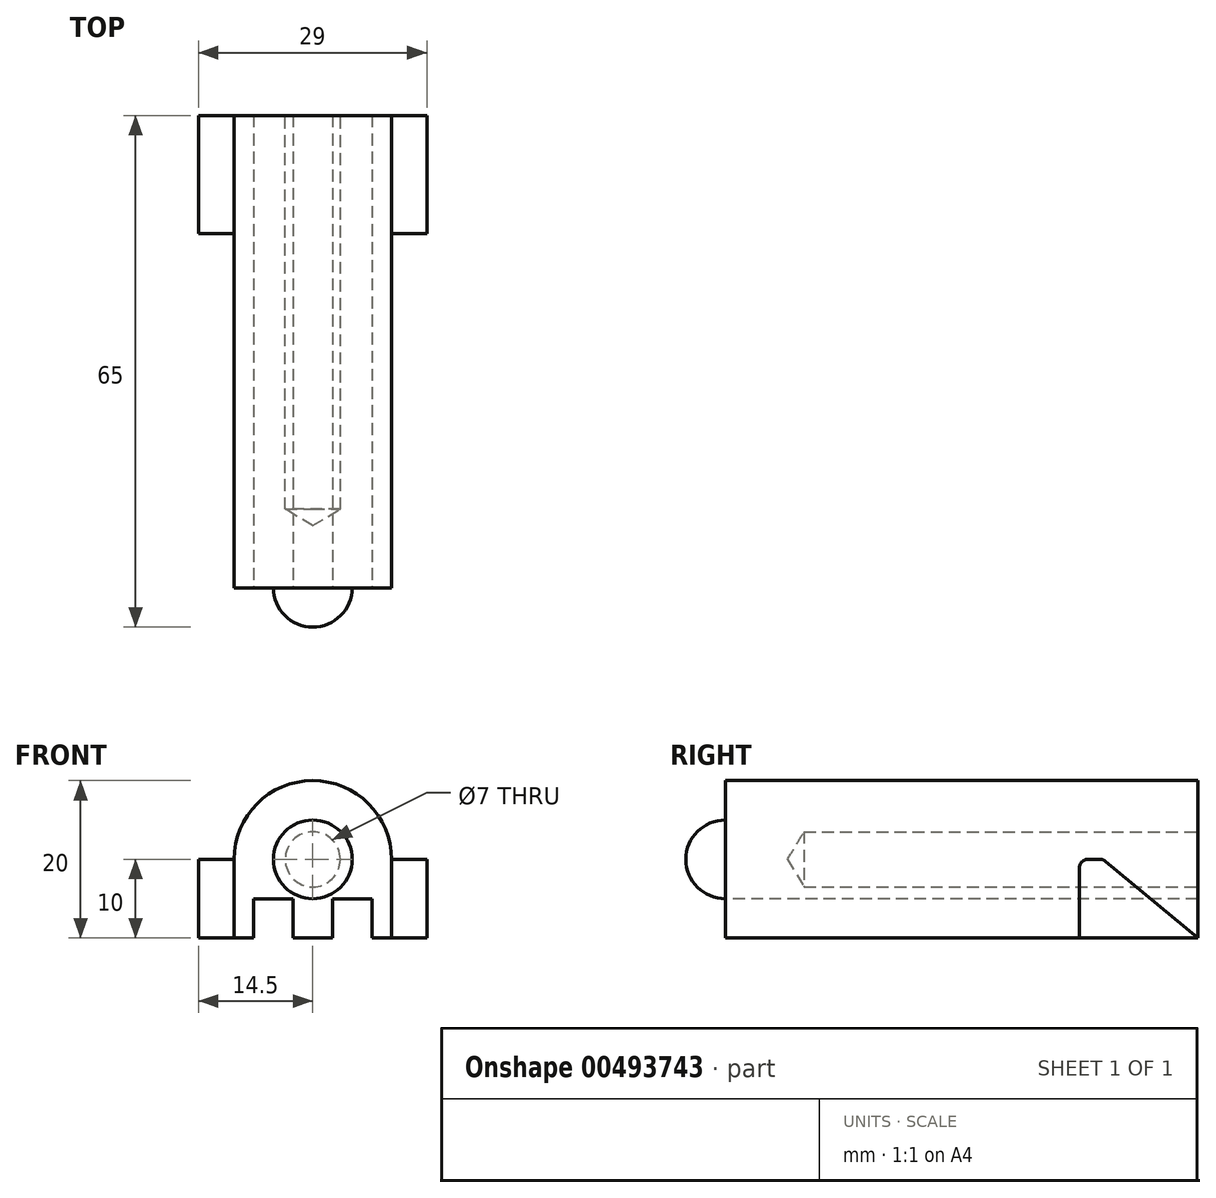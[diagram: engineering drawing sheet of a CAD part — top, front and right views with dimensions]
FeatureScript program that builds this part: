
annotation { "Feature Type Name" : "Feature", "Feature Type Description" : "" }
export const myFeature = defineFeature(function(context is Context, id is Id, definition is map)
    precondition{}
    {
        {
            var Q0;
            Q0=qCreatedBy(makeId("Front.planeOp"),FACE);
            var sketch = newSketch(context, id + "F0", { "sketchPlane" : qUnion([Q0])});
            skLineSegment(sketch, "E0.bottom", {"start": v(-10, 0) * mm, "end": v(-7.5, 0) * mm});
            skLineSegment(sketch, "E0.left", {"start": v(-10, 0) * mm, "end": v(-10, 10) * mm});
            skLineSegment(sketch, "E0.right", {"start": v(10, 0) * mm, "end": v(10, 10) * mm});
            skArc(sketch, "E1", {"start": v(10, 10) * mm, "mid": v(0, 20) * mm, "end": v(-10, 10) * mm});
            skLineSegment(sketch, "E2.top", {"start": v(-2.5, 5) * mm, "end": v(-7.5, 5) * mm});
            skLineSegment(sketch, "E2.left", {"start": v(-2.5, 0) * mm, "end": v(-2.5, 5) * mm});
            skLineSegment(sketch, "E2.right", {"start": v(-7.5, 0) * mm, "end": v(-7.5, 5) * mm});
            skLineSegment(sketch, "E3.bottom", {"start": v(2.5, 5) * mm, "end": v(7.5, 5) * mm});
            skLineSegment(sketch, "E3.left", {"start": v(2.5, 5) * mm, "end": v(2.5, 0) * mm});
            skLineSegment(sketch, "E3.right", {"start": v(7.5, 5) * mm, "end": v(7.5, 0) * mm});
            skLineSegment(sketch, "E4.trimOffspring", {"start": v(7.5, 0) * mm, "end": v(10, 0) * mm});
            skLineSegment(sketch, "E5.trimOffspring", {"start": v(-2.5, 0) * mm, "end": v(2.5, 0) * mm});
            skSolve(sketch);
        }
        {
            var Q0;
            Q0 = qSketchRegion(id + "F0", true);
            extrude(context, id + "F1", {"entities" : qUnion([Q0]), "oppositeDirection" : true, "depth" : 60 * mm});
        }
        {
            var Q0;
            Q0=qCreatedBy(makeId("Right.planeOp"),FACE);
            var sketch = newSketch(context, id + "F2", { "sketchPlane" : qUnion([Q0])});
            skArc(sketch, "E6", {"start": v(0, 15) * mm, "mid": v(-5, 10) * mm, "end": v(0, 5) * mm});
            skLineSegment(sketch, "E7", {"start": v(0, 15) * mm, "end": v(0, 5) * mm});
            skSolve(sketch);
        }
        {
            var Q0;
            Q0=makeQuery(id+"F2.imprint","IMPRINT",FACE,{"disambiguationData":[TD([[makeQuery(id+"F2.imprint","IMPRINT",EDGE,{"derivedFrom":sQuery(id+"F2.wireOp",EDGE,"E6")}),1.0]])]});
            var Q1;
            Q1=sQuery(id+"F2.wireOp",EDGE,"E7");
            revolve(context, id + "F3", {"operationType" : NewBodyOperationType.ADD, "entities" : qUnion([Q0]), "axis" : qUnion([Q1]), "revolveType" : RevolveType.FULL});
        }
        {
            var Q0;
            Q0=makeQuery(id+"F1.opExtrude","CAP_FACE",FACE,{"disambiguationData":[OSD([sQuery(id+"F0.wireOp",EDGE,"E0.bottom"),sQuery(id+"F0.wireOp",EDGE,"E0.left"),sQuery(id+"F0.wireOp",EDGE,"E0.right"),sQuery(id+"F0.wireOp",EDGE,"E1"),sQuery(id+"F0.wireOp",EDGE,"E2.top"),sQuery(id+"F0.wireOp",EDGE,"E2.left"),sQuery(id+"F0.wireOp",EDGE,"E2.right"),sQuery(id+"F0.wireOp",EDGE,"E3.bottom"),sQuery(id+"F0.wireOp",EDGE,"E3.left"),sQuery(id+"F0.wireOp",EDGE,"E3.right"),sQuery(id+"F0.wireOp",EDGE,"E4.trimOffspring"),sQuery(id+"F0.wireOp",EDGE,"E5.trimOffspring")])],"isStart":false});
            var sketch = newSketch(context, id + "F4", { "sketchPlane" : qUnion([Q0])});
            skCircle(sketch, "E8", {"center": v(0, 10) * mm, "radius": 3.5 * mm});
            skSolve(sketch);
        }
        {
            var Q0;
            Q0=sQuery(id+"F4.wireOp",VERTEX,"E8.center");
            var Q1;
            Q1=makeQuery(id+"F1.opExtrude","SWEPT_BODY",BODY,{"disambiguationData":[OSD([sQuery(id+"F0.wireOp",EDGE,"E0.bottom"),sQuery(id+"F0.wireOp",EDGE,"E0.left"),sQuery(id+"F0.wireOp",EDGE,"E0.right"),sQuery(id+"F0.wireOp",EDGE,"E1"),sQuery(id+"F0.wireOp",EDGE,"E2.top"),sQuery(id+"F0.wireOp",EDGE,"E2.left"),sQuery(id+"F0.wireOp",EDGE,"E2.right"),sQuery(id+"F0.wireOp",EDGE,"E3.bottom"),sQuery(id+"F0.wireOp",EDGE,"E3.left"),sQuery(id+"F0.wireOp",EDGE,"E3.right"),sQuery(id+"F0.wireOp",EDGE,"E4.trimOffspring"),sQuery(id+"F0.wireOp",EDGE,"E5.trimOffspring")])]});
            hole(context, id + "F5", {"style" : HoleStyle.SIMPLE, "endStyle" : HoleEndStyle.BLIND, "holeDiameter" : 7 * mm, "holeDepth" : 50 * mm, "isTappedThrough" : true, "tappedDepth" : 12 * mm, "tapClearance" : 3, "locations" : qUnion([Q0]), "scope" : qUnion([Q1])});
        }
        {
            var Q0;
            Q0=makeQuery(id+"F1.opExtrude","SWEPT_FACE",FACE,{"disambiguationData":[OSD([sQuery(id+"F0.wireOp",EDGE,"E0.right")])]});
            var sketch = newSketch(context, id + "F6", { "sketchPlane" : qUnion([Q0])});
            skLineSegment(sketch, "E9", {"start": v(60, 0) * mm, "end": v(45, 0) * mm});
            skLineSegment(sketch, "E10", {"start": v(45, 0) * mm, "end": v(45, 10) * mm});
            skLineSegment(sketch, "E11", {"start": v(45, 10) * mm, "end": v(48, 10) * mm});
            skLineSegment(sketch, "E12", {"start": v(48, 10) * mm, "end": v(60, 0) * mm});
            skSolve(sketch);
        }
        {
            var Q0;
            Q0 = qSketchRegion(id + "F6", true);
            extrude(context, id + "F7", {"entities" : qUnion([Q0]), "operationType" : NewBodyOperationType.ADD, "depth" : 4.5 * mm});
        }
        {
            var Q0;
            Q0=makeQuery(id+"F1.opExtrude","SWEPT_FACE",FACE,{"disambiguationData":[OSD([sQuery(id+"F0.wireOp",EDGE,"E0.left")])]});
            var sketch = newSketch(context, id + "F8", { "sketchPlane" : qUnion([Q0])});
            skLineSegment(sketch, "E13", {"start": v(-60, 0) * mm, "end": v(-45, 0) * mm});
            skLineSegment(sketch, "E14", {"start": v(-45, 0) * mm, "end": v(-45, 10) * mm});
            skLineSegment(sketch, "E15", {"start": v(-45, 10) * mm, "end": v(-48, 10) * mm});
            skLineSegment(sketch, "E16", {"start": v(-48, 10) * mm, "end": v(-60, 0) * mm});
            skSolve(sketch);
        }
        {
            var Q0;
            Q0 = qSketchRegion(id + "F8", true);
            extrude(context, id + "F9", {"entities" : qUnion([Q0]), "operationType" : NewBodyOperationType.ADD, "depth" : 4.5 * mm});
        }
        {
            var Q0;
            Q0=makeQuery(id+"F7.opExtrude","SWEPT_EDGE",EDGE,{"disambiguationData":[OSD([sQuery(id+"F0.wireOp",EDGE,"E0.right"),sQuery(id+"F0.wireOp",EDGE,"E1"),sQuery(id+"F6.wireOp",EDGE,"E10"),sQuery(id+"F6.wireOp",EDGE,"E11")])]});
            var Q1;
            Q1=makeQuery(id+"F7.opExtrude","SWEPT_EDGE",EDGE,{"disambiguationData":[OSD([sQuery(id+"F0.wireOp",EDGE,"E0.right"),sQuery(id+"F0.wireOp",EDGE,"E1"),sQuery(id+"F6.wireOp",EDGE,"E11"),sQuery(id+"F6.wireOp",EDGE,"E12")])]});
            var Q2;
            Q2=makeQuery(id+"F9.opExtrude","SWEPT_EDGE",EDGE,{"disambiguationData":[OSD([sQuery(id+"F0.wireOp",EDGE,"E0.left"),sQuery(id+"F0.wireOp",EDGE,"E1"),sQuery(id+"F8.wireOp",EDGE,"E14"),sQuery(id+"F8.wireOp",EDGE,"E15")])]});
            var Q3;
            Q3=makeQuery(id+"F9.opExtrude","SWEPT_EDGE",EDGE,{"disambiguationData":[OSD([sQuery(id+"F0.wireOp",EDGE,"E0.left"),sQuery(id+"F0.wireOp",EDGE,"E1"),sQuery(id+"F8.wireOp",EDGE,"E15"),sQuery(id+"F8.wireOp",EDGE,"E16")])]});
            fillet(context, id + "F10", {"entities" : qUnion([Q0, Q1, Q2, Q3]), "radius" : 1 * mm, "tangentPropagation" : true, "allowEdgeOverflow" : false});
        }
    });
